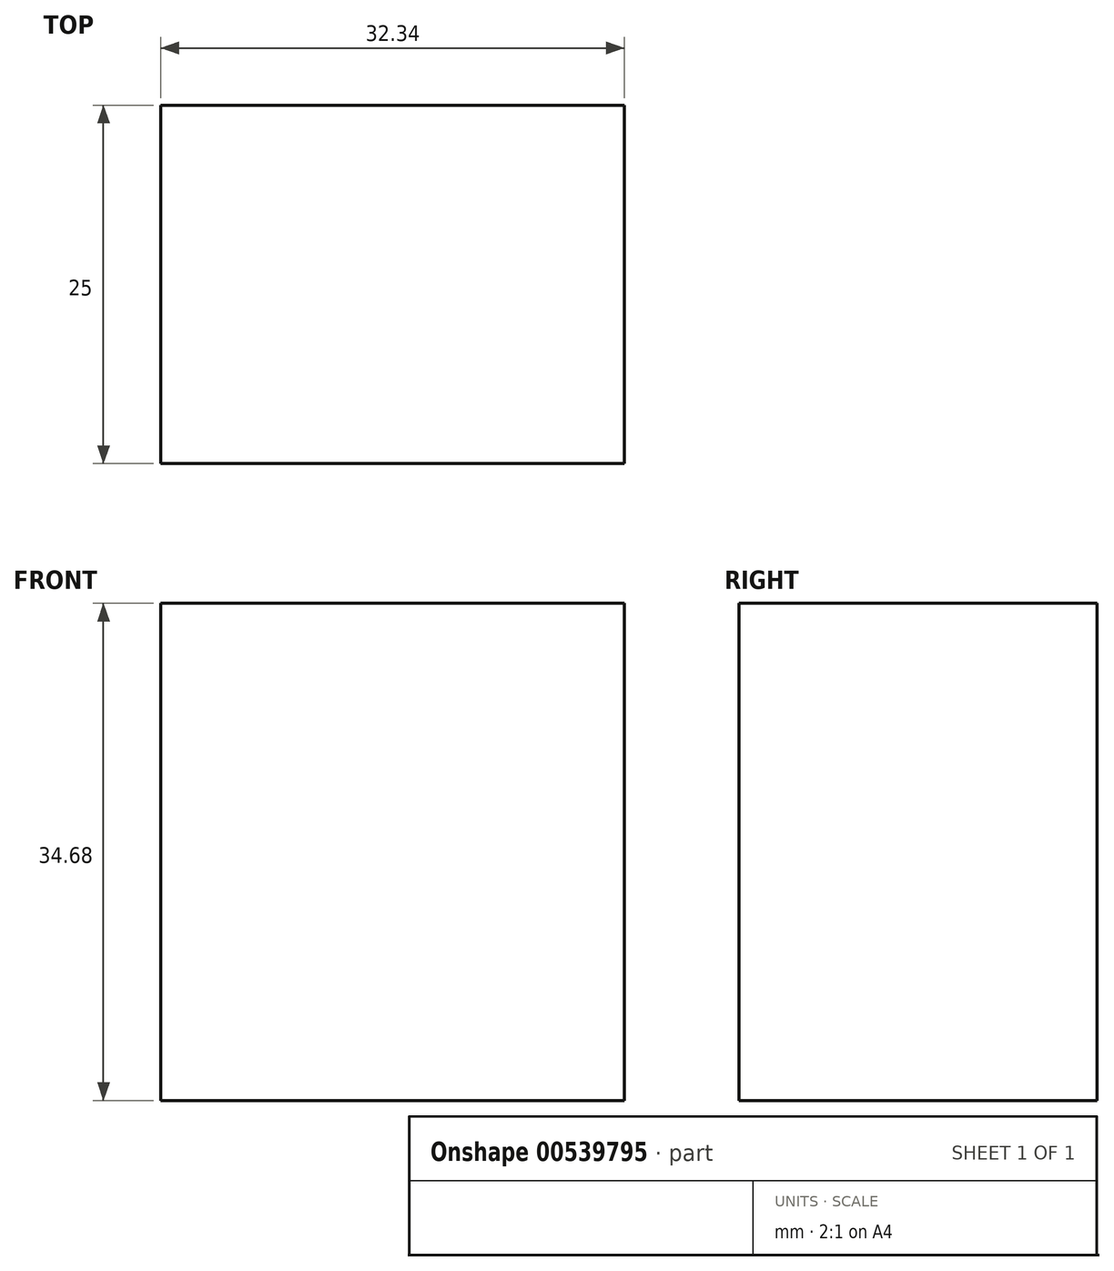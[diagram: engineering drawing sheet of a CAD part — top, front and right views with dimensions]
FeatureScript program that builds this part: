
annotation { "Feature Type Name" : "Feature", "Feature Type Description" : "" }
export const myFeature = defineFeature(function(context is Context, id is Id, definition is map)
    precondition{}
    {
        {
            var Q0;
            Q0=qCreatedBy(makeId("Front.planeOp"),FACE);
            var sketch = newSketch(context, id + "F0", { "sketchPlane" : qUnion([Q0])});
            skLineSegment(sketch, "E0.bottom", {"start": v(-54.06, 34.68) * mm, "end": v(-21.72, 34.68) * mm});
            skLineSegment(sketch, "E0.top", {"start": v(-54.06, 0) * mm, "end": v(-21.72, 0) * mm});
            skLineSegment(sketch, "E0.left", {"start": v(-54.06, 34.68) * mm, "end": v(-54.06, 0) * mm});
            skLineSegment(sketch, "E0.right", {"start": v(-21.72, 34.68) * mm, "end": v(-21.72, 0) * mm});
            skSolve(sketch);
        }
        {
            var Q0;
            Q0 = qSketchRegion(id + "F0", true);
            extrude(context, id + "F1", {"entities" : qUnion([Q0]), "depth" : 25 * mm, "offsetDistance" : 25 * mm});
        }
    });
